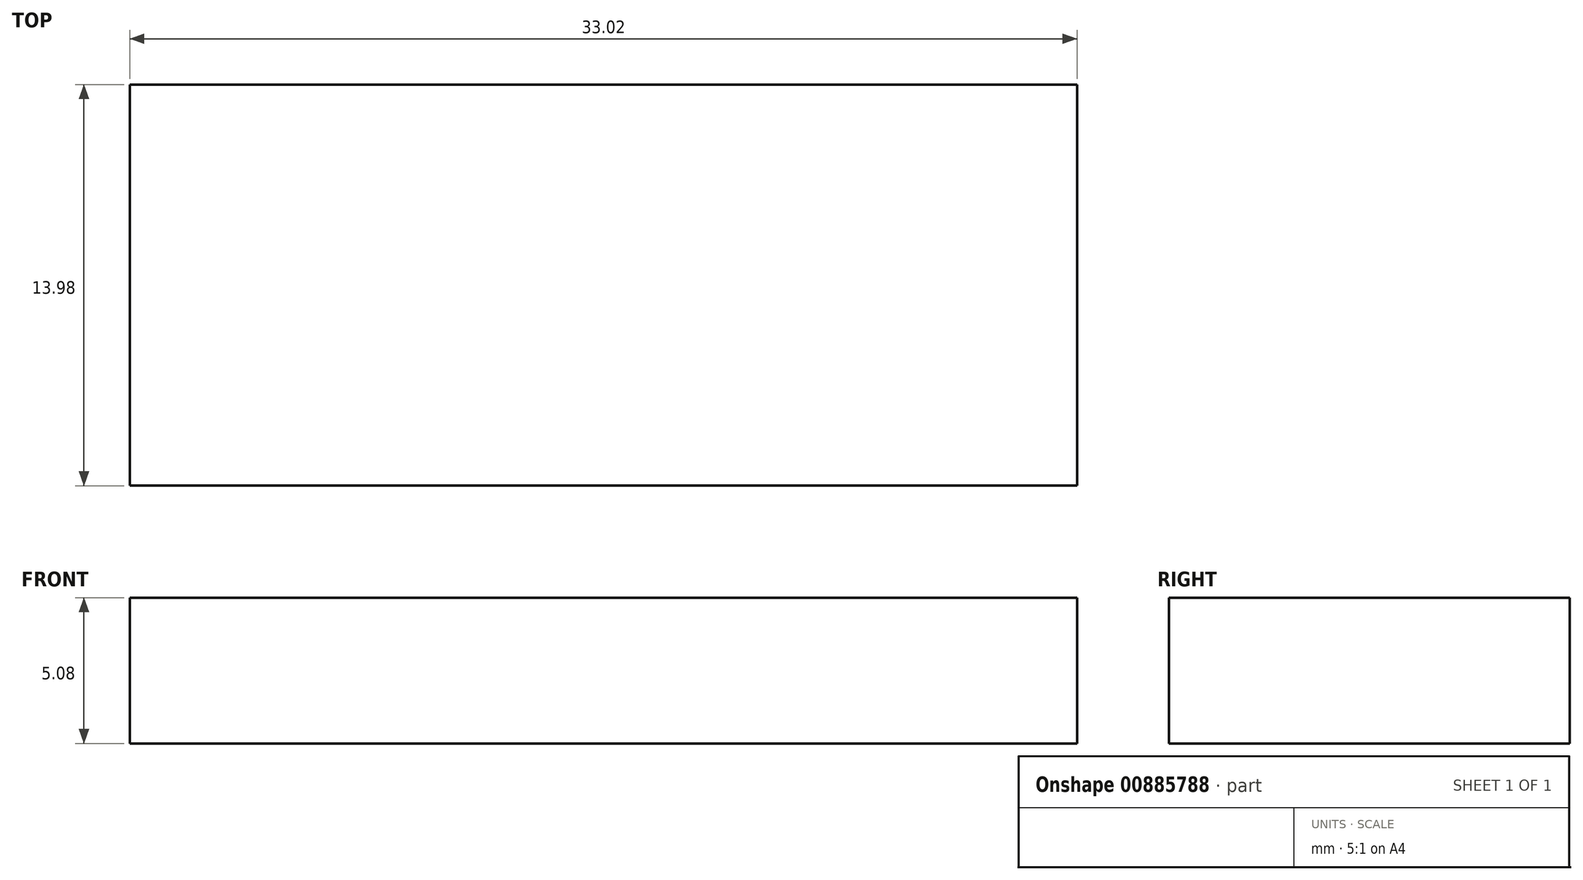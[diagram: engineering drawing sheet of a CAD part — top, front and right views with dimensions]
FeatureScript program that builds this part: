
annotation { "Feature Type Name" : "Feature", "Feature Type Description" : "" }
export const myFeature = defineFeature(function(context is Context, id is Id, definition is map)
    precondition{}
    {
        {
            var Q0;
            Q0=qCreatedBy(makeId("Top.planeOp"),FACE);
            var sketch = newSketch(context, id + "F0", { "sketchPlane" : qUnion([Q0])});
            skLineSegment(sketch, "E0.bottom", {"start": v(16.51, -6.98) * mm, "end": v(-16.51, -6.99) * mm});
            skLineSegment(sketch, "E0.top", {"start": v(16.51, 6.99) * mm, "end": v(-16.51, 6.99) * mm});
            skLineSegment(sketch, "E0.left", {"start": v(16.51, -6.98) * mm, "end": v(16.51, 6.99) * mm});
            skLineSegment(sketch, "E0.right", {"start": v(-16.51, -6.99) * mm, "end": v(-16.51, 6.99) * mm});
            skPoint(sketch, "E0.middle", {"position": v(0, 0) * mm});
            skSolve(sketch);
        }
        {
            var Q0;
            Q0 = qSketchRegion(id + "F0", true);
            extrude(context, id + "F1", {"entities" : qUnion([Q0]), "depth" : 5.08 * mm, "offsetDistance" : 25.4 * mm});
        }
    });
